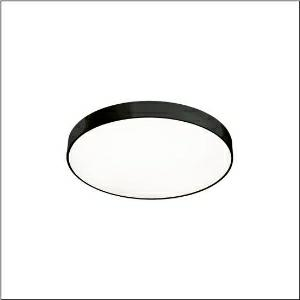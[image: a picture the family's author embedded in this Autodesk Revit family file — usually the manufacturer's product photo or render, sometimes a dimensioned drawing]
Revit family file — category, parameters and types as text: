
# Revit family: round_21_m_51mr36fd0321b
name_source: partatom
category: Lighting Fixtures
units: mm (PartAtom-declared; Revit-internal decimal feet)

## family parameters
Cut with Voids When Loaded = No
Host = Face
Light Source = No
Part Type = Normal
Room Calculation Point = No
Round Connector Dimension = Use Diameter
Shared = No

## types (1)
- Round 21 M (1 x LED, 7500 lm, 54.9 W, 3000K)
    Apparent Load = 55 VA
    CIE Flux Codes = 49 80 96 100 100
    Color Rendering = 80
    Color Temperature = 3000K
    Default Elevation = 1800 mm
    Description = Round 21 M, wall and ceiling luminaire, primary optical cover: cover, of PMMA, opal, light emission: direct distribution, primary light characteristic: symmetric, installation type: suspended mounting, surface-mounted, LED, rated luminous flux: 7.500lm, luminous efficacy: 137lm/W, light colour: 830, colour temperature: 3000K, control gear: DALI 2, with terminal, 5-pole, mains connection: 230V, AC, 50/60Hz, rated input power: 54.8W, housing, of aluminium, coated, black, diameter: 600mm, height: 62mm, protection rating (complete): IP40, insulation class (complete): insulation class I (protective earthing), certification: CE, impact resistance: IK04, permissible operating ambient temperature: -10..+35°C, packaging unit: 1 piece
    Height = 87 mm
    Lamp = 1 x LED
    Lamp Light Flux = 7500 lm
    Lamp Power = 54.9 W
    Lamp count = 1
    Length = 600 mm
    Luminous efficacy = 137 lm/W
    Manufacturer = Siteco
    ModVariant = No
    Model = 51MR36FD0321B
    Mounting Place = Ceiling
    Mounting Type = Surface mounted
    Number of Poles = 1
    OnlyDefault = Yes
    Power Factor = 1
    Product Name = Round 21 M
    Product group = wall and ceiling luminaire
    ProductGroupID = 304
    Protection Class = Protection class I
    Protection Degree = IP 40
    RLX_Detail_Level = 1
    RLX_Emergency_Light_Flux = 0 lm
    RLX_Emergency_Type = 0
    RLX_Emergency_Type_DB = No
    RlxData = <blob elided: 17737 chars, md5=84bc5859>
    Socket = socket
    Standby Power = 0 W
    System Light Flux = 7500 lm
    System Power = 55 W
    Type Comments = Product without accessories
    Type Image = l_1258332.jpg
    URL = http://relux.com
    VarID = ---
    Voltage = 0 V
    Weight = 0.00 kg
    Width = 0 mm  [stored 0 ft]

note: [stored X ft] marks values corroborated as IEEE doubles in the binary element streams (Revit-internal decimal feet)

## geometry (parser evidence)
native form markers: Blend x4, Sweep x10
no freeform markers — native parametric forms only
